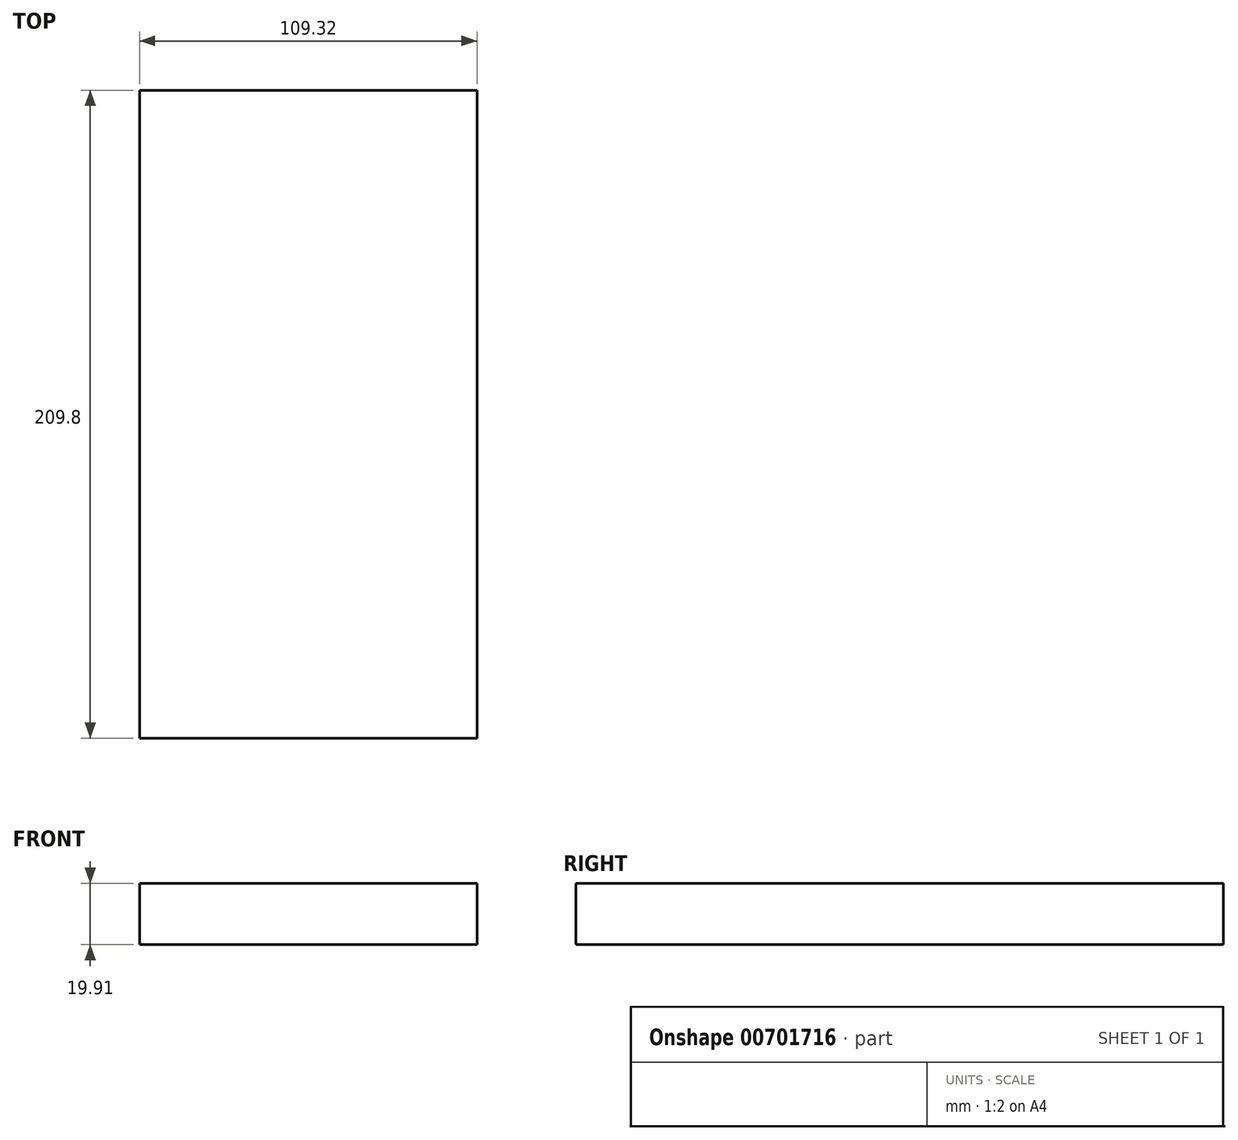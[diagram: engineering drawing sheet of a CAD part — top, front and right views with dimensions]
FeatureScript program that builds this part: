
annotation { "Feature Type Name" : "Feature", "Feature Type Description" : "" }
export const myFeature = defineFeature(function(context is Context, id is Id, definition is map)
    precondition{}
    {
        {
            var Q0;
            Q0=qCreatedBy(makeId("Front.planeOp"),FACE);
            var sketch = newSketch(context, id + "F0", { "sketchPlane" : qUnion([Q0])});
            skLineSegment(sketch, "E0.bottom", {"start": v(-52.82, 11.52) * mm, "end": v(56.5, 11.52) * mm});
            skLineSegment(sketch, "E0.top", {"start": v(-52.82, -8.39) * mm, "end": v(56.5, -8.39) * mm});
            skLineSegment(sketch, "E0.left", {"start": v(-52.82, 11.52) * mm, "end": v(-52.82, -8.39) * mm});
            skLineSegment(sketch, "E0.right", {"start": v(56.5, 11.52) * mm, "end": v(56.5, -8.39) * mm});
            skLineSegment(sketch, "E1.bottom", {"start": v(43.97, 11.52) * mm, "end": v(87.85, 11.52) * mm});
            skLineSegment(sketch, "E1.top", {"start": v(43.97, 43.05) * mm, "end": v(87.85, 43.05) * mm});
            skLineSegment(sketch, "E1.left", {"start": v(43.97, 11.52) * mm, "end": v(43.97, 43.05) * mm});
            skLineSegment(sketch, "E1.right", {"start": v(87.85, 11.52) * mm, "end": v(87.85, 43.05) * mm});
            skLineSegment(sketch, "E2.bottom", {"start": v(87.85, 30.65) * mm, "end": v(131.35, 30.65) * mm});
            skLineSegment(sketch, "E2.top", {"start": v(87.85, 43.05) * mm, "end": v(131.35, 43.05) * mm});
            skLineSegment(sketch, "E2.left", {"start": v(87.85, 30.65) * mm, "end": v(87.85, 43.05) * mm});
            skLineSegment(sketch, "E2.right", {"start": v(131.35, 30.65) * mm, "end": v(131.35, 43.05) * mm});
            skFitSpline(sketch, "E3", {"points": [v(-52.82, 11.52) * mm, v(43.97, 43.05) * mm], "startDerivative": vector(77.96, 75.54) * mm, "endDerivative": vector(101.23, 2.44) * mm});
            skSolve(sketch);
        }
        {
            var Q0;
            {var subQ1=sQuery(id+"F0.wireOp",EDGE,"E0.bottom");Q0=makeQuery(id+"F0.imprint","IMPRINT",FACE,{"disambiguationData":[TD([[makeQuery(id+"F0.imprint","IMPRINT",EDGE,{"derivedFrom":subQ1}),-1.0]])]});}
            extrude(context, id + "F1", {"entities" : qUnion([Q0]), "endBound" : BoundingType.SYMMETRIC, "depth" : 209.8 * mm, "offsetDistance" : 25.4 * mm});
        }
    });
